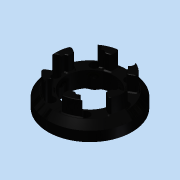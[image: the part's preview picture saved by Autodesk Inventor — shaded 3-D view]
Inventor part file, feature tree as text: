
AUTODESK INVENTOR PART (.ipt)
format: ipt  version: 2015 (Build 190159000, 159)  size: 1,019,392 bytes
history: native  units: in
note: dims shown in document units (in); Inventor stores cm internally (conversion verified against a paired STEP export)
features: extrude x8, chamfer x7, projected_geometry x7, sketch x4, fillet x4, other x1, pattern_circular x1, plane x1, split x1
ambient origin geometry x8: Origin, YZ Plane, XZ Plane, XY Plane, X Axis, Y Axis, Z Axis, Center Point
bodies: Solid1 (feature_tree)
feature tree (34):
  other  "wheelinsertsketch.ipt"
  extrude  "Extrusion1"  Depth=0.35in TaperAngle=0.0deg
  extrude  "Extrusion2"  Depth=0.25in TaperAngle=0.0deg
  chamfer  "Chamfer1"  Distance=0.25in Angle=45.0deg
  chamfer  "Chamfer6"  Distance=0.1625in Angle=45.0deg
  extrude  "Extrusion6"  Depth=0.375in
  extrude  "Extrusion9"  Depth=0.375in
  sketch  "Sketch6"  dims[d3=2.15in d4=0.25in d5=0.0in d6=0.25in d7=0.125in d8=45.0deg d42=0.1625in d43=0.125in d44=45.0deg]
  extrude  "Extrusion7"  Depth=0.375in
  chamfer  "Chamfer9"  Distance=0.375in
  fillet  "Fillet6"  Radius=0.375in
  fillet  "Fillet7"  Radius=0.01in
  extrude  "Extrusion10"  Depth=0.01in
  chamfer  "Chamfer10"  Distance=0.01in
  extrude  "Extrusion11"  Depth=2.3622in TaperAngle=360.0deg
  chamfer  "Chamfer11"  Distance=0.02in
  chamfer  "Chamfer13"  Distance=0.047in Angle=45.0deg
  pattern_circular  "Circular Pattern1"  [2 undecoded]
  chamfer  "Chamfer12"  Distance=0.145in
  fillet  "Fillet8"  Radius=0.05in
  plane  "Work Plane1"
  split  "Split1"
  extrude  "Extrusion12"  Depth=0.05in TaperAngle=45.0deg
  fillet  "Fillet9"  Radius=0.0197in
  sketch  "Sketch5"  dims[d0=0.3937in d1=0.35in d2=0.0in]
  projected_geometry  "Projected Loop3"
  projected_geometry  "Projected Loop4"
  projected_geometry  "Projected Loop5"
  projected_geometry  "Projected Loop12"
  sketch  "Sketch9"  dims[d45=1.0in d46=0.0in d47=0.375in]
  projected_geometry  "Projected Loop13"
  sketch  "Sketch11"  dims[d48=0.375in d49=0.375in d50=0.375in d51=0.375in d52=0.375in d53=0.01in d54=0.0in d67=0.01in d68=0.01in d69=2.3622in d71=360.0deg d73=0.02in d74=0.0in d78=0.047in d79=0.125in d80=45.0deg d81=0.15in d82=0.145in d83=0.05in d84=0.0in d85=0.05in d86=0.125in d87=45.0deg d89=0.0197in d90=0.0in d91=0.0197in d92=0.125in d93=45.0deg d94=0.0098in d95=0.125in d96=45.0deg d97=2.0in d98=2.3622in d99=360.0deg d101=0.0in d102=0.11in d103=0.115in d104=0.0in d105=0.0in d106=0.0118in d107=0.125in d108=45.0deg d109=0.26in d113=2.3622in d115=360.0deg d118=0.0197in d119=0.16in]
  projected_geometry  "Project Cut Edges2"
  projected_geometry  "Project Cut Edges3"
note: 2 required parameter values undecoded (feature->parameter linkage not recoverable at this tier; creation-order binding heuristic only, values carry confidence <= 0.55)
